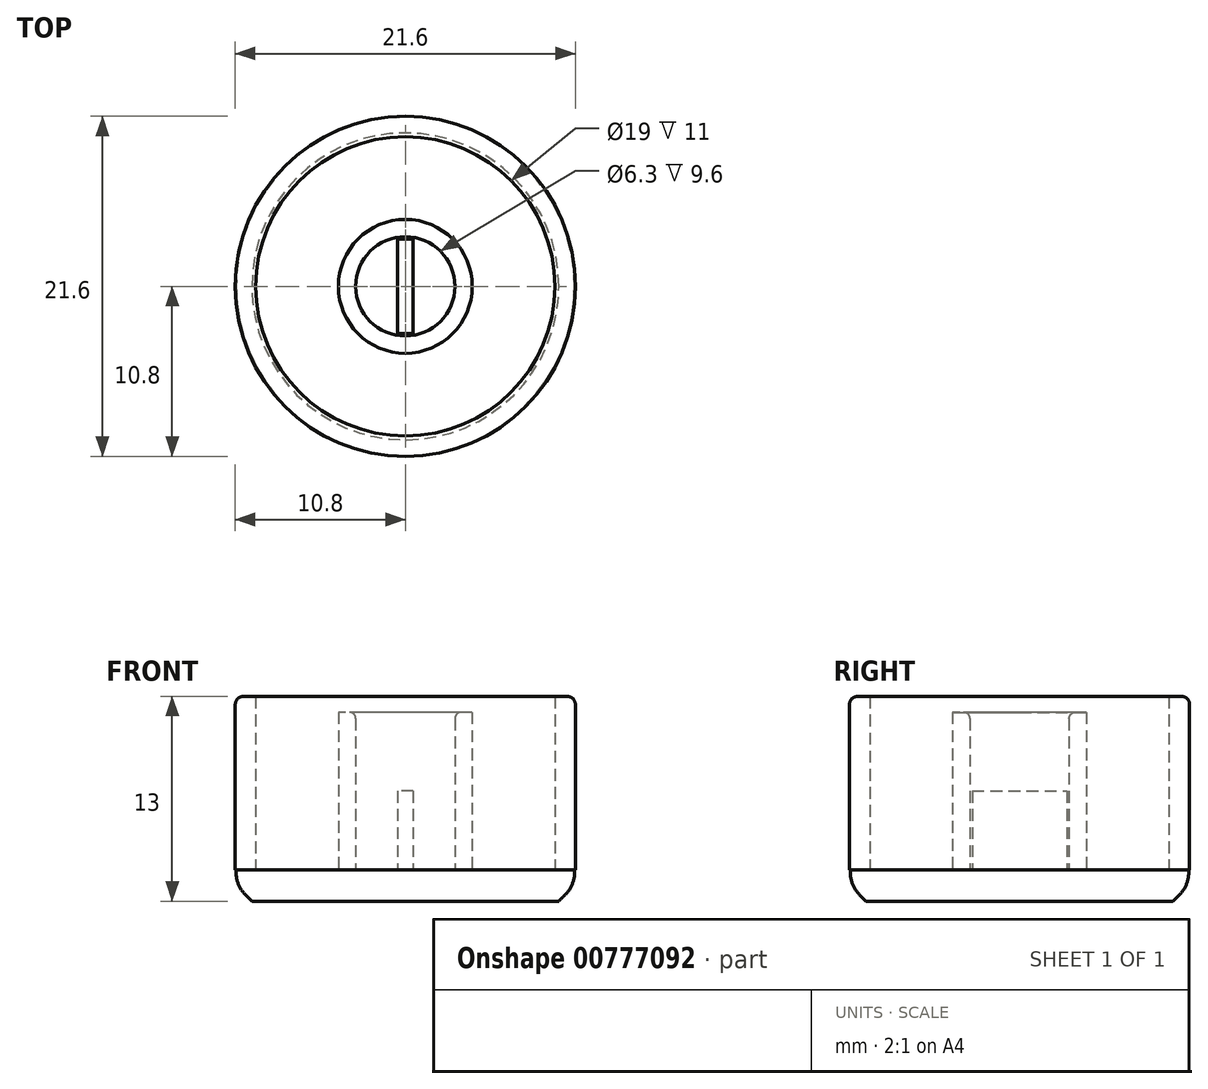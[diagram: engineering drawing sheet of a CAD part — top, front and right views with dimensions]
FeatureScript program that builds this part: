
annotation { "Feature Type Name" : "Feature", "Feature Type Description" : "" }
export const myFeature = defineFeature(function(context is Context, id is Id, definition is map)
    precondition{}
    {
        {
            var Q0;
            Q0=qCreatedBy(makeId("Top.planeOp"),FACE);
            var sketch = newSketch(context, id + "F0", { "sketchPlane" : qUnion([Q0])});
            skCircle(sketch, "E0", {"center": v(0, 0) * mm, "radius": 3.15 * mm});
            skCircle(sketch, "E1", {"center": v(0, 0) * mm, "radius": 4.25 * mm});
            skSolve(sketch);
        }
        {
            var Q0;
            Q0=makeQuery(id+"F0.imprint","IMPRINT",FACE,{"disambiguationData":[TD([[makeQuery(id+"F0.imprint","IMPRINT",EDGE,{"derivedFrom":sQuery(id+"F0.wireOp",EDGE,"E0")}),-1.0]])]});
            extrude(context, id + "F1", {"entities" : qUnion([Q0]), "depth" : 10 * mm, "offsetDistance" : 25 * mm});
        }
        {
            var Q0;
            Q0=qCreatedBy(makeId("Top.planeOp"),FACE);
            var sketch = newSketch(context, id + "F2", { "sketchPlane" : qUnion([Q0])});
            skCircle(sketch, "E2", {"center": v(0, 0) * mm, "radius": 9.5 * mm});
            skCircle(sketch, "E3.0", {"center": v(0, 0) * mm, "radius": 10.8 * mm});
            skSolve(sketch);
        }
        {
            var Q0;
            Q0=makeQuery(id+"F2.imprint","IMPRINT",FACE,{"disambiguationData":[TD([[makeQuery(id+"F2.imprint","IMPRINT",EDGE,{"derivedFrom":sQuery(id+"F2.wireOp",EDGE,"E2")}),-1.0]])]});
            extrude(context, id + "F3", {"entities" : qUnion([Q0]), "depth" : 11 * mm, "offsetDistance" : 25 * mm});
        }
        {
            var Q0;
            Q0=qCreatedBy(makeId("Top.planeOp"),FACE);
            var sketch = newSketch(context, id + "F4", { "sketchPlane" : qUnion([Q0])});
            skCircle(sketch, "E4", {"center": v(0, 0) * mm, "radius": 10.75 * mm});
            skSolve(sketch);
        }
        {
            var Q0;
            Q0 = qSketchRegion(id + "F4", true);
            extrude(context, id + "F5", {"entities" : qUnion([Q0]), "oppositeDirection" : true, "depth" : 2 * mm, "offsetDistance" : 25 * mm});
        }
        {
            var Q0;
            Q0=makeQuery(id+"F5.opExtrude","CAP_FACE",FACE,{"disambiguationData":[OSD([sQuery(id+"F4.wireOp",EDGE,"E4")])],"isStart":true});
            var sketch = newSketch(context, id + "F6", { "sketchPlane" : qUnion([Q0])});
            skLineSegment(sketch, "E5.bottom", {"start": v(0.5, -3) * mm, "end": v(-0.5, -3) * mm});
            skLineSegment(sketch, "E5.top", {"start": v(0.5, 3) * mm, "end": v(-0.5, 3) * mm});
            skLineSegment(sketch, "E5.left", {"start": v(0.5, -3) * mm, "end": v(0.5, 3) * mm});
            skLineSegment(sketch, "E5.right", {"start": v(-0.5, -3) * mm, "end": v(-0.5, 3) * mm});
            skPoint(sketch, "E5.middle", {"position": v(0, 0) * mm});
            skSolve(sketch);
        }
        {
            var Q0;
            Q0=makeQuery(id+"F6.imprint","IMPRINT",FACE,{"disambiguationData":[TD([[makeQuery(id+"F6.imprint","IMPRINT",EDGE,{"derivedFrom":sQuery(id+"F6.wireOp",EDGE,"E5.bottom")}),-1.0]])]});
            extrude(context, id + "F7", {"entities" : qUnion([Q0]), "depth" : 5 * mm, "offsetDistance" : 25 * mm});
        }
        {
            var Q0;
            Q0=makeQuery(id+"F5.opExtrude","CAP_EDGE",EDGE,{"disambiguationData":[OSD([sQuery(id+"F4.wireOp",EDGE,"E4")])],"isStart":false});
            chamfer(context, id + "F8", {"entities" : qUnion([Q0]), "width" : 1 * mm, "tangentPropagation" : true});
        }
        {
            var Q0;
            {var subQ0=sQuery(id+"F4.wireOp",EDGE,"E4");Q0=makeQuery(id+"F8.opChamfer","BLEND_EDGE",EDGE,{"blendedFrom":[makeQuery(id+"F5.opExtrude","CAP_EDGE",EDGE,{"disambiguationData":[OSD([subQ0])],"isStart":false}),makeQuery(id+"F5.opExtrude","SWEPT_FACE",FACE,{"disambiguationData":[OSD([subQ0])]})],"blendedInto":[makeQuery(id+"F5.opExtrude","SWEPT_FACE",FACE,{"disambiguationData":[OSD([subQ0])]})]});}
            fillet(context, id + "F9", {"entities" : qUnion([Q0]), "radius" : 2 * mm, "tangentPropagation" : true, "allowEdgeOverflow" : false});
        }
        {
            var Q0;
            Q0=makeQuery(id+"F3.opExtrude","CAP_EDGE",EDGE,{"disambiguationData":[OSD([sQuery(id+"F2.wireOp",EDGE,"E3.0")])],"isStart":false});
            fillet(context, id + "F10", {"entities" : qUnion([Q0]), "radius" : 0.5 * mm, "tangentPropagation" : true, "allowEdgeOverflow" : false});
        }
        {
            var Q0;
            Q0=makeQuery(id+"F1.opExtrude","CAP_EDGE",EDGE,{"disambiguationData":[OSD([sQuery(id+"F0.wireOp",EDGE,"E0")])],"isStart":false});
            fillet(context, id + "F11", {"entities" : qUnion([Q0]), "radius" : 0.4 * mm, "tangentPropagation" : true, "allowEdgeOverflow" : false});
        }
    });
